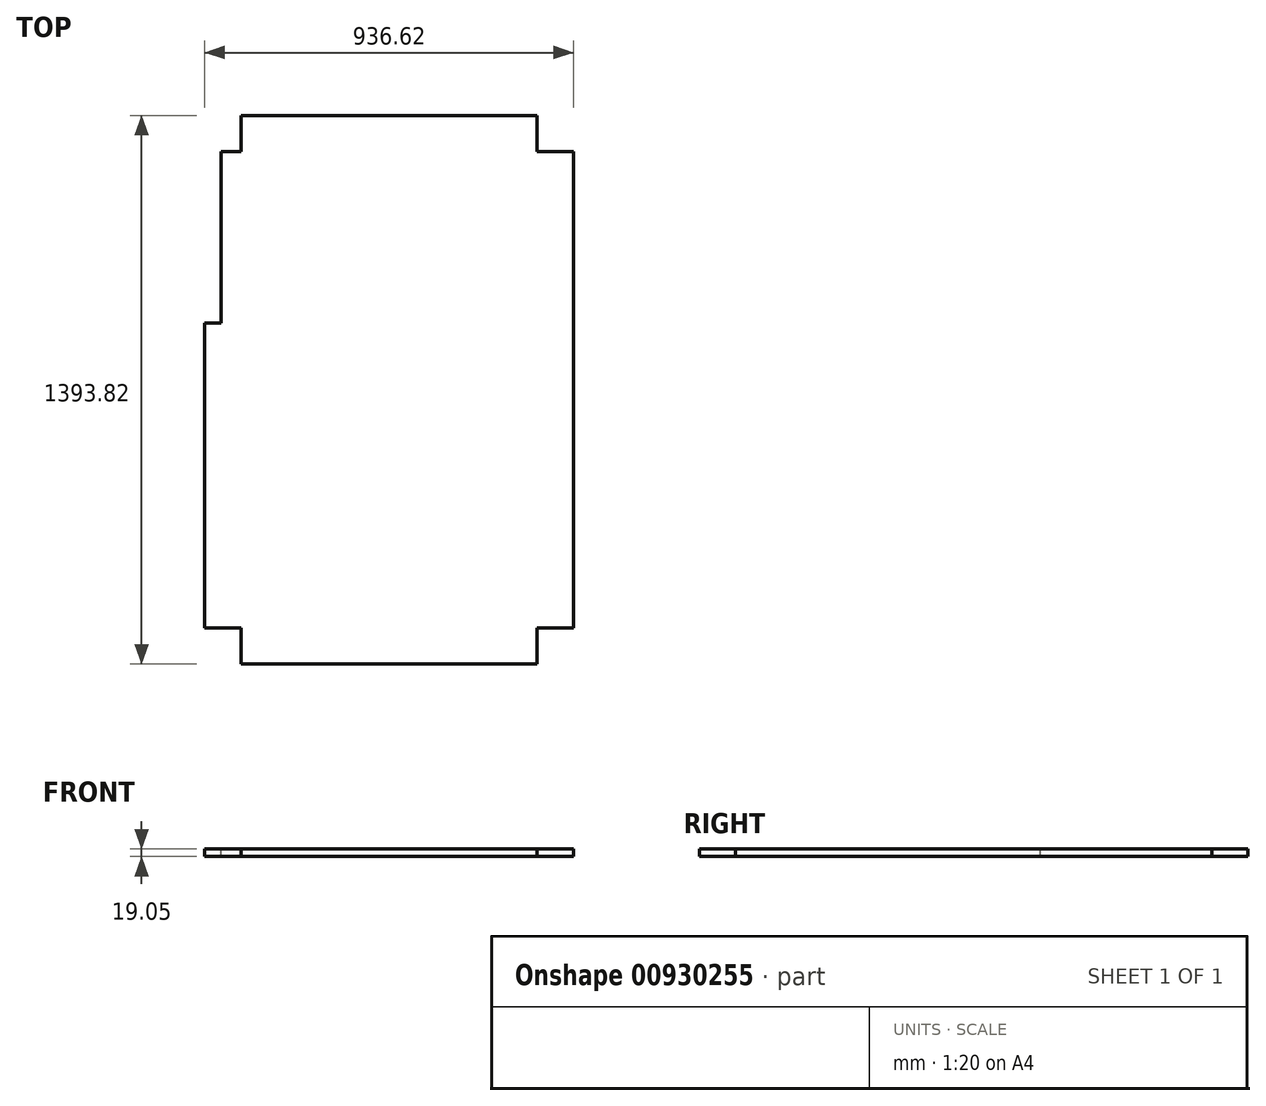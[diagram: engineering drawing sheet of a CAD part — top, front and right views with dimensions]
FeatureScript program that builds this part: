
annotation { "Feature Type Name" : "Feature", "Feature Type Description" : "" }
export const myFeature = defineFeature(function(context is Context, id is Id, definition is map)
    precondition{}
    {
        {
            var Q0;
            Q0=qCreatedBy(makeId("Top.planeOp"),FACE);
            var sketch = newSketch(context, id + "F0", { "sketchPlane" : qUnion([Q0])});
            skLineSegment(sketch, "E0.bottom", {"start": v(468.31, -696.91) * mm, "end": v(-468.31, -696.91) * mm});
            skLineSegment(sketch, "E0.top", {"start": v(468.31, 696.91) * mm, "end": v(-468.31, 696.91) * mm});
            skLineSegment(sketch, "E0.left", {"start": v(468.31, -696.91) * mm, "end": v(468.31, 696.91) * mm});
            skLineSegment(sketch, "E0.right", {"start": v(-468.31, -696.91) * mm, "end": v(-468.31, 696.91) * mm});
            skPoint(sketch, "E0.middle", {"position": v(0, 0) * mm});
            skSolve(sketch);
        }
        {
            var Q0;
            Q0=qSketchRegion(id+"F0",true);
            extrude(context, id + "F1", {"entities" : qUnion([Q0]), "depth" : 19.05 * mm});
        }
        {
            var Q0;
            Q0=makeQuery(id+"F1.opExtrude","CAP_FACE",FACE,{"disambiguationData":[OSD([sQuery(id+"F0.wireOp",EDGE,"E0.bottom"),sQuery(id+"F0.wireOp",EDGE,"E0.top"),sQuery(id+"F0.wireOp",EDGE,"E0.left"),sQuery(id+"F0.wireOp",EDGE,"E0.right")])],"isStart":false});
            var sketch = newSketch(context, id + "F2", { "sketchPlane" : qUnion([Q0])});
            skLineSegment(sketch, "E1.bottom", {"start": v(-468.31, 696.91) * mm, "end": v(-376.24, 696.91) * mm});
            skLineSegment(sketch, "E1.top", {"start": v(-468.31, 604.84) * mm, "end": v(-376.24, 604.84) * mm});
            skLineSegment(sketch, "E1.left", {"start": v(-468.31, 696.91) * mm, "end": v(-468.31, 604.84) * mm});
            skLineSegment(sketch, "E1.right", {"start": v(-376.24, 696.91) * mm, "end": v(-376.24, 604.84) * mm});
            skLineSegment(sketch, "E2.bottom", {"start": v(468.31, 696.91) * mm, "end": v(376.24, 696.91) * mm});
            skLineSegment(sketch, "E2.top", {"start": v(468.31, 604.84) * mm, "end": v(376.24, 604.84) * mm});
            skLineSegment(sketch, "E2.left", {"start": v(468.31, 696.91) * mm, "end": v(468.31, 604.84) * mm});
            skLineSegment(sketch, "E2.right", {"start": v(376.24, 696.91) * mm, "end": v(376.24, 604.84) * mm});
            skLineSegment(sketch, "E3.bottom", {"start": v(468.31, -696.91) * mm, "end": v(376.24, -696.91) * mm});
            skLineSegment(sketch, "E3.top", {"start": v(468.31, -604.84) * mm, "end": v(376.24, -604.84) * mm});
            skLineSegment(sketch, "E3.left", {"start": v(468.31, -696.91) * mm, "end": v(468.31, -604.84) * mm});
            skLineSegment(sketch, "E3.right", {"start": v(376.24, -696.91) * mm, "end": v(376.24, -604.84) * mm});
            skLineSegment(sketch, "E4.bottom", {"start": v(-468.31, -696.91) * mm, "end": v(-376.24, -696.91) * mm});
            skLineSegment(sketch, "E4.top", {"start": v(-468.31, -604.84) * mm, "end": v(-376.24, -604.84) * mm});
            skLineSegment(sketch, "E4.left", {"start": v(-468.31, -696.91) * mm, "end": v(-468.31, -604.84) * mm});
            skLineSegment(sketch, "E4.right", {"start": v(-376.24, -696.91) * mm, "end": v(-376.24, -604.84) * mm});
            skSolve(sketch);
        }
        {
            var Q0;
            Q0=qSketchRegion(id+"F2",true);
            extrude(context, id + "F3", {"entities" : qUnion([Q0]), "operationType" : NewBodyOperationType.REMOVE, "endBound" : BoundingType.THROUGH_ALL, "oppositeDirection" : true, "depth" : 25.4 * mm});
        }
        {
            var Q0;
            Q0=makeQuery(id+"F1.opExtrude","CAP_FACE",FACE,{"disambiguationData":[OSD([sQuery(id+"F0.wireOp",EDGE,"E0.bottom"),sQuery(id+"F0.wireOp",EDGE,"E0.top"),sQuery(id+"F0.wireOp",EDGE,"E0.left"),sQuery(id+"F0.wireOp",EDGE,"E0.right")])],"isStart":false});
            var sketch = newSketch(context, id + "F4", { "sketchPlane" : qUnion([Q0])});
            skLineSegment(sketch, "E5.bottom", {"start": v(-468.31, 604.84) * mm, "end": v(-427.04, 604.84) * mm});
            skLineSegment(sketch, "E5.top", {"start": v(-468.31, 169.86) * mm, "end": v(-427.04, 169.86) * mm});
            skLineSegment(sketch, "E5.left", {"start": v(-468.31, 604.84) * mm, "end": v(-468.31, 169.86) * mm});
            skLineSegment(sketch, "E5.right", {"start": v(-427.04, 604.84) * mm, "end": v(-427.04, 169.86) * mm});
            skSolve(sketch);
        }
        {
            var Q0;
            Q0=qSketchRegion(id+"F4",true);
            extrude(context, id + "F5", {"entities" : qUnion([Q0]), "operationType" : NewBodyOperationType.REMOVE, "endBound" : BoundingType.THROUGH_ALL, "oppositeDirection" : true, "depth" : 25.4 * mm});
        }
    });
